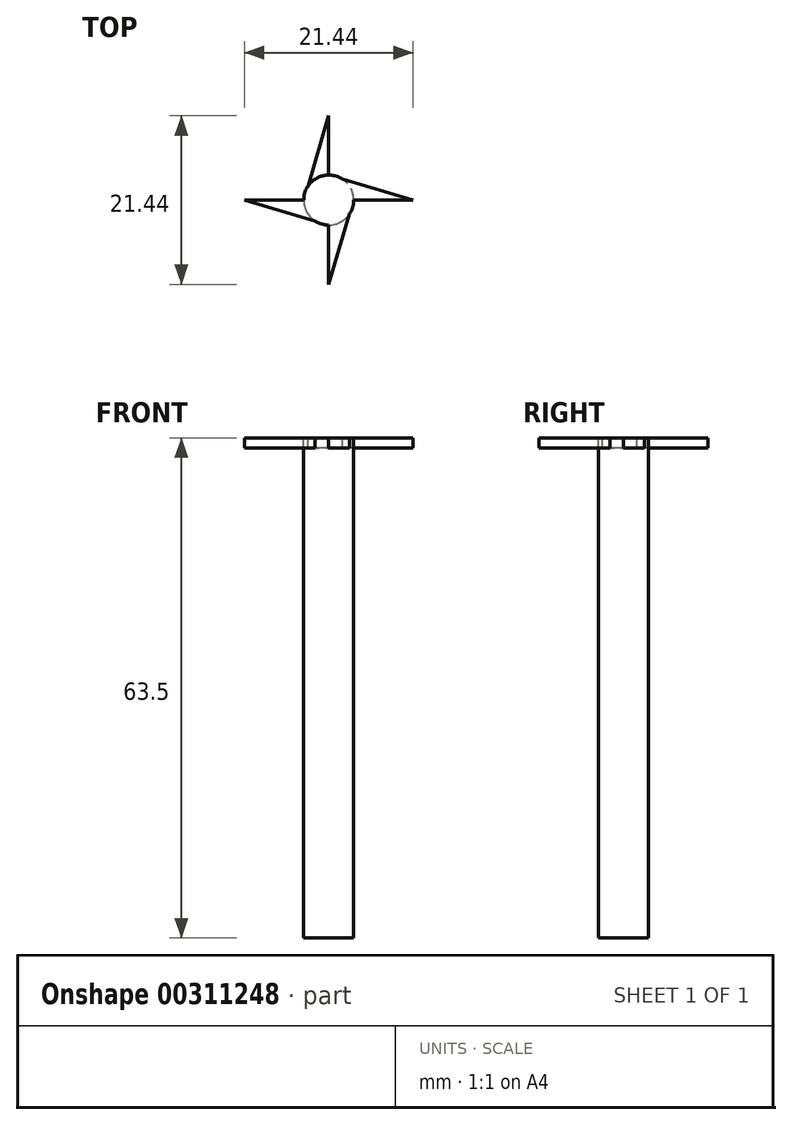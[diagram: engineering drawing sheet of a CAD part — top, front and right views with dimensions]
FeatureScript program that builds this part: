
annotation { "Feature Type Name" : "Feature", "Feature Type Description" : "" }
export const myFeature = defineFeature(function(context is Context, id is Id, definition is map)
    precondition{}
    {
        {
            var Q0;
            Q0=qCreatedBy(makeId("Top.planeOp"),FACE);
            var sketch = newSketch(context, id + "F0", { "sketchPlane" : qUnion([Q0])});
            skCircle(sketch, "E0", {"center": v(0, 0) * mm, "radius": 3.18 * mm});
            skSolve(sketch);
        }
        {
            var Q0;
            Q0=makeQuery(id+"F0.imprint","IMPRINT",FACE,{"disambiguationData":[TD([[makeQuery(id+"F0.imprint","IMPRINT",EDGE,{"derivedFrom":sQuery(id+"F0.wireOp",EDGE,"E0")}),1.0]])]});
            extrude(context, id + "F1", {"entities" : qUnion([Q0]), "depth" : 31.75 * mm, "hasSecondDirection" : true, "secondDirectionOppositeDirection" : true, "secondDirectionDepth" : 31.75 * mm});
        }
        {
            var Q0;
            Q0=makeQuery(id+"F1.opExtrude","CAP_FACE",FACE,{"disambiguationData":[OSD([sQuery(id+"F0.wireOp",EDGE,"E0")])],"isStart":false});
            var sketch = newSketch(context, id + "F2", { "sketchPlane" : qUnion([Q0])});
            skLineSegment(sketch, "E1", {"start": v(-3.18, 0) * mm, "end": v(0, 10.72) * mm});
            skLineSegment(sketch, "E2", {"start": v(0, 10.72) * mm, "end": v(0, 3.18) * mm});
            skLineSegment(sketch, "E3", {"start": v(0, 3.18) * mm, "end": v(10.72, 0) * mm});
            skLineSegment(sketch, "E4", {"start": v(10.72, 0) * mm, "end": v(3.18, 0) * mm});
            skLineSegment(sketch, "E5", {"start": v(3.18, 0) * mm, "end": v(0, -10.72) * mm});
            skLineSegment(sketch, "E6", {"start": v(0, -10.72) * mm, "end": v(0, -3.18) * mm});
            skLineSegment(sketch, "E7", {"start": v(0, -3.17) * mm, "end": v(-10.72, 0) * mm});
            skLineSegment(sketch, "E8", {"start": v(-10.72, 0) * mm, "end": v(-3.17, 0) * mm});
            skSolve(sketch);
        }
        {
            var Q0;
            {var subQ0=sQuery(id+"F2.wireOp",EDGE,"E2");Q0=makeQuery(id+"F2.imprint","IMPRINT",FACE,{"disambiguationData":[TD([[makeQuery(id+"F2.imprint","IMPRINT",EDGE,{"derivedFrom":subQ0}),-1.0]])]});}
            extrude(context, id + "F3", {"entities" : qUnion([Q0]), "oppositeDirection" : true, "depth" : 1.27 * mm});
        }
        {
            var Q0;
            {var subQ0=sQuery(id+"F2.wireOp",EDGE,"E8");Q0=makeQuery(id+"F2.imprint","IMPRINT",FACE,{"disambiguationData":[TD([[makeQuery(id+"F2.imprint","IMPRINT",EDGE,{"derivedFrom":subQ0}),-1.0]])]});}
            extrude(context, id + "F4", {"entities" : qUnion([Q0]), "operationType" : NewBodyOperationType.ADD, "oppositeDirection" : true, "depth" : 1.27 * mm});
        }
        {
            var Q0;
            {var subQ0=sQuery(id+"F2.wireOp",EDGE,"E6");Q0=makeQuery(id+"F2.imprint","IMPRINT",FACE,{"disambiguationData":[TD([[makeQuery(id+"F2.imprint","IMPRINT",EDGE,{"derivedFrom":subQ0}),-1.0]])]});}
            extrude(context, id + "F5", {"entities" : qUnion([Q0]), "operationType" : NewBodyOperationType.ADD, "oppositeDirection" : true, "depth" : 1.27 * mm});
        }
        {
            var Q0;
            {var subQ0=sQuery(id+"F2.wireOp",EDGE,"E4");Q0=makeQuery(id+"F2.imprint","IMPRINT",FACE,{"disambiguationData":[TD([[makeQuery(id+"F2.imprint","IMPRINT",EDGE,{"derivedFrom":subQ0}),-1.0]])]});}
            extrude(context, id + "F6", {"entities" : qUnion([Q0]), "operationType" : NewBodyOperationType.ADD, "oppositeDirection" : true, "depth" : 1.27 * mm});
        }
    });
